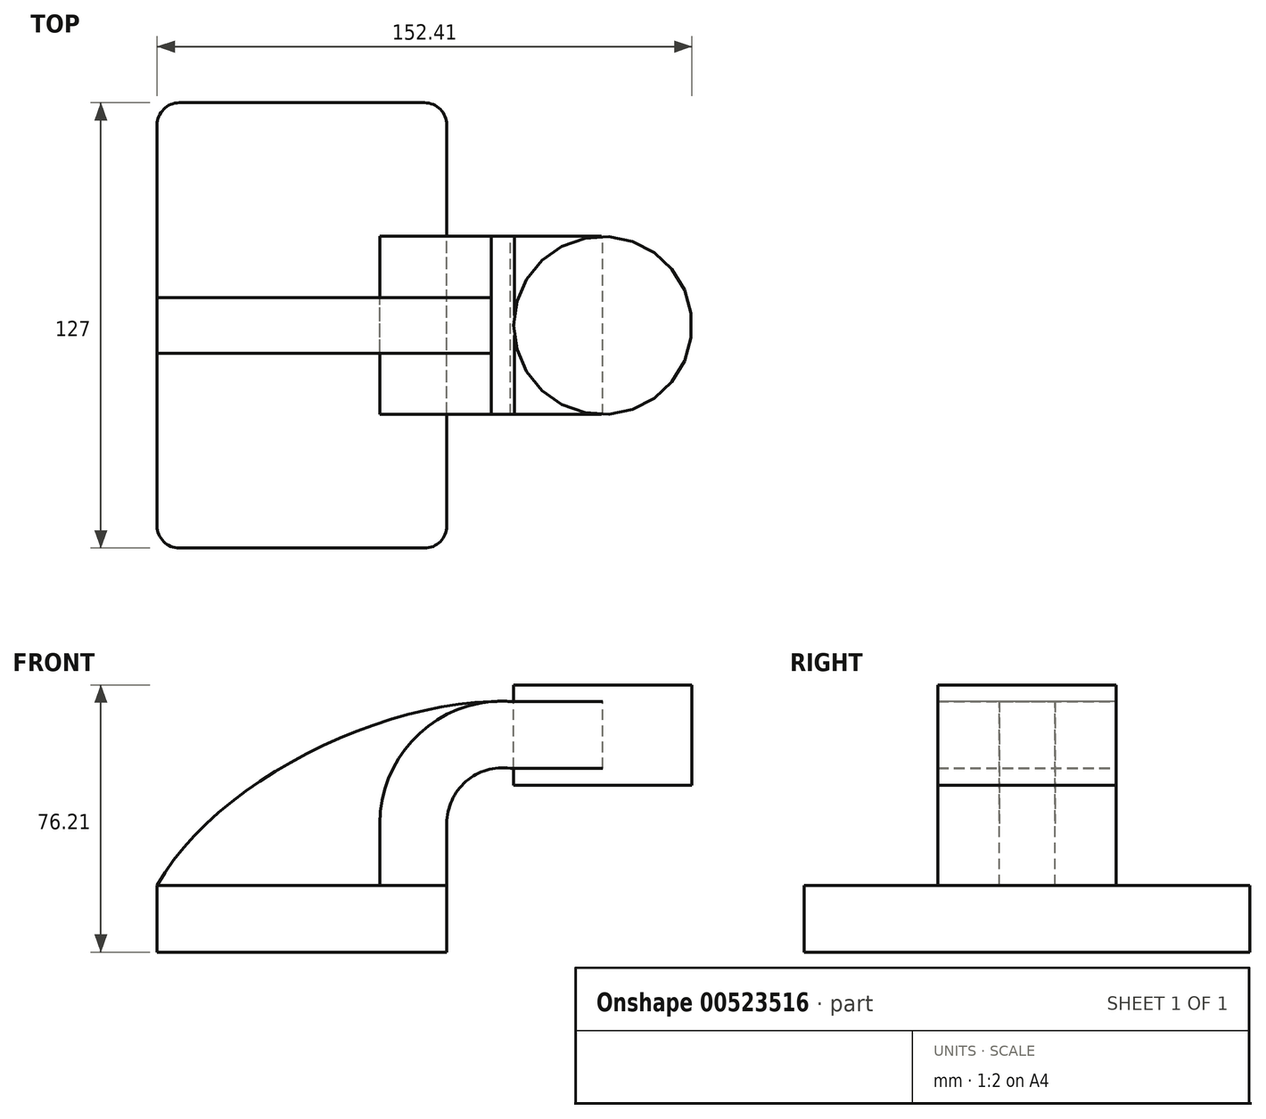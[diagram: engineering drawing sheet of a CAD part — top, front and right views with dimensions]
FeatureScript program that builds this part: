
annotation { "Feature Type Name" : "Feature", "Feature Type Description" : "" }
export const myFeature = defineFeature(function(context is Context, id is Id, definition is map)
    precondition{}
    {
        {
            var Q0;
            Q0=qCreatedBy(makeId("Front.planeOp"),FACE);
            var sketch = newSketch(context, id + "F0", { "sketchPlane" : qUnion([Q0])});
            skLineSegment(sketch, "E0.bottom", {"start": v(41.27, 9.53) * mm, "end": v(-41.28, 9.53) * mm});
            skLineSegment(sketch, "E0.top", {"start": v(41.28, -9.52) * mm, "end": v(-41.27, -9.52) * mm});
            skLineSegment(sketch, "E0.left", {"start": v(41.28, 9.53) * mm, "end": v(41.28, -9.52) * mm});
            skLineSegment(sketch, "E0.right", {"start": v(-41.28, 9.53) * mm, "end": v(-41.28, -9.52) * mm});
            skPoint(sketch, "E0.middle", {"position": v(0, 0) * mm});
            skLineSegment(sketch, "E1.bottom", {"start": v(111.13, 38.1) * mm, "end": v(60.33, 38.1) * mm});
            skLineSegment(sketch, "E1.top", {"start": v(111.13, 66.68) * mm, "end": v(60.33, 66.68) * mm});
            skLineSegment(sketch, "E1.left", {"start": v(111.13, 38.1) * mm, "end": v(111.13, 66.68) * mm});
            skLineSegment(sketch, "E1.right", {"start": v(60.33, 38.1) * mm, "end": v(60.33, 66.68) * mm});
            skPoint(sketch, "E1.middle", {"position": v(85.72, 52.39) * mm});
            skLineSegment(sketch, "E2", {"start": v(41.27, 9.53) * mm, "end": v(41.27, 27.16) * mm});
            skArc(sketch, "E3", {"start": v(41.28, 27.16) * mm, "mid": v(46.75, 39.15) * mm, "end": v(59.4, 42.88) * mm});
            skArc(sketch, "E4.1", {"start": v(22.23, 27.16) * mm, "mid": v(33.66, 53) * mm, "end": v(60.48, 61.93) * mm});
            skLineSegment(sketch, "E4.2", {"start": v(22.22, 9.53) * mm, "end": v(22.22, 27.16) * mm});
            skLineSegment(sketch, "E5", {"start": v(85.73, 38.1) * mm, "end": v(85.72, 66.68) * mm});
            skFitSpline(sketch, "E6", {"points": [v(-41.28, 9.53) * mm, v(60.48, 61.93) * mm], "startDerivative": vector(50.11, 90.24) * mm, "endDerivative": vector(107.61, -4.62) * mm});
            skLineSegment(sketch, "E7", {"start": v(59.4, 42.88) * mm, "end": v(85.72, 42.88) * mm});
            skLineSegment(sketch, "E8", {"start": v(60.48, 61.93) * mm, "end": v(85.72, 61.93) * mm});
            skSolve(sketch);
        }
        {
            var Q0;
            Q0=makeQuery(id+"F0.imprint","IMPRINT",FACE,{"disambiguationData":[TD([[makeQuery(id+"F0.imprint","IMPRINT",EDGE,{"derivedFrom":sQuery(id+"F0.wireOp",EDGE,"E0.top")}),-1.0]])]});
            extrude(context, id + "F1", {"entities" : qUnion([Q0]), "endBound" : BoundingType.SYMMETRIC, "depth" : 127 * mm, "offsetDistance" : 25.4 * mm});
        }
        {
            var Q0;
            {var subQ3=sQuery(id+"F0.wireOp",EDGE,"E4.2");Q0=makeQuery(id+"F0.imprint","IMPRINT",FACE,{"disambiguationData":[TD([[makeQuery(id+"F0.imprint","IMPRINT",EDGE,{"derivedFrom":subQ3}),1.0]])]});}
            extrude(context, id + "F2", {"entities" : qUnion([Q0]), "endBound" : BoundingType.SYMMETRIC, "depth" : 15.88 * mm, "offsetDistance" : 25.4 * mm});
        }
        {
            var Q0;
            {var subQ0=sQuery(id+"F0.wireOp",EDGE,"E2");Q0=makeQuery(id+"F0.imprint","IMPRINT",FACE,{"disambiguationData":[TD([[makeQuery(id+"F0.imprint","IMPRINT",EDGE,{"derivedFrom":subQ0}),1.0]])]});}
            var Q1;
            {var subQ5=sQuery(id+"F0.wireOp",EDGE,"E8");Q1=makeQuery(id+"F0.imprint","IMPRINT",FACE,{"disambiguationData":[TD([[makeQuery(id+"F0.imprint","IMPRINT",EDGE,{"derivedFrom":subQ5}),-1.0]])]});}
            extrude(context, id + "F3", {"entities" : qUnion([Q0, Q1]), "endBound" : BoundingType.SYMMETRIC, "depth" : 50.8 * mm, "offsetDistance" : 25.4 * mm});
        }
        {
            var Q0;
            {var subQ0=sQuery(id+"F0.wireOp",EDGE,"E1.left");Q0=makeQuery(id+"F0.imprint","IMPRINT",FACE,{"disambiguationData":[TD([[makeQuery(id+"F0.imprint","IMPRINT",EDGE,{"derivedFrom":subQ0}),1.0]])]});}
            var Q1;
            Q1=sQuery(id+"F0.wireOp",EDGE,"E5");
            revolve(context, id + "F4", {"entities" : qUnion([Q0]), "axis" : qUnion([Q1]), "revolveType" : RevolveType.FULL});
        }
        {
            var Q0;
            Q0=makeQuery(id+"F1.opExtrude","CAP_EDGE",EDGE,{"disambiguationData":[OSD([sQuery(id+"F0.wireOp",EDGE,"E0.right")])],"isStart":false});
            var Q1;
            Q1=makeQuery(id+"F1.opExtrude","CAP_EDGE",EDGE,{"disambiguationData":[OSD([sQuery(id+"F0.wireOp",EDGE,"E0.left")])],"isStart":false});
            var Q2;
            Q2=makeQuery(id+"F1.opExtrude","CAP_EDGE",EDGE,{"disambiguationData":[OSD([sQuery(id+"F0.wireOp",EDGE,"E0.left")])],"isStart":true});
            var Q3;
            Q3=makeQuery(id+"F1.opExtrude","CAP_EDGE",EDGE,{"disambiguationData":[OSD([sQuery(id+"F0.wireOp",EDGE,"E0.right")])],"isStart":true});
            fillet(context, id + "F5", {"entities" : qUnion([Q0, Q1, Q2, Q3]), "radius" : 6.35 * mm, "tangentPropagation" : true, "allowEdgeOverflow" : false});
        }
    });
